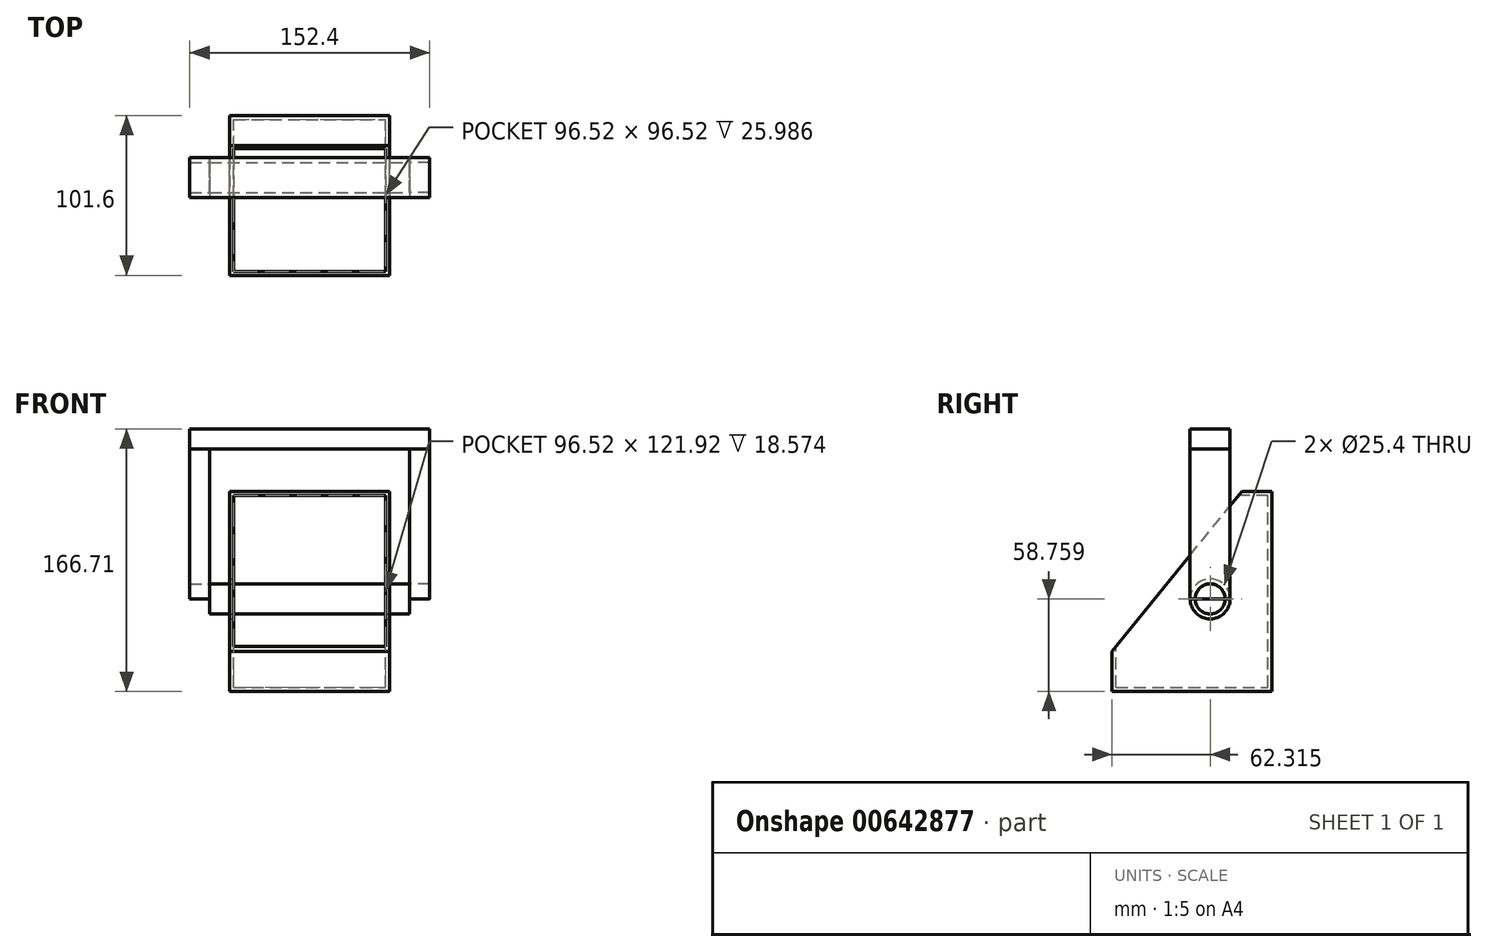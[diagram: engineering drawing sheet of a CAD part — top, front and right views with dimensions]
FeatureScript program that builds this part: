
annotation { "Feature Type Name" : "Feature", "Feature Type Description" : "" }
export const myFeature = defineFeature(function(context is Context, id is Id, definition is map)
    precondition{}
    {
        {
            var Q0;
            Q0=qCreatedBy(makeId("Right.planeOp"),FACE);
            var sketch = newSketch(context, id + "F0", { "sketchPlane" : qUnion([Q0])});
            skLineSegment(sketch, "E0", {"start": v(0, 0) * mm, "end": v(101.6, 0) * mm});
            skLineSegment(sketch, "E1", {"start": v(101.6, 0) * mm, "end": v(101.6, 127) * mm});
            skLineSegment(sketch, "E2", {"start": v(101.6, 127) * mm, "end": v(82.55, 127) * mm});
            skLineSegment(sketch, "E3", {"start": v(0, 0) * mm, "end": v(0, 25.4) * mm});
            skLineSegment(sketch, "E4", {"start": v(0, 25.4) * mm, "end": v(82.55, 127) * mm});
            skSolve(sketch);
        }
        {
            var Q0;
            Q0=makeQuery(id+"F0.imprint","IMPRINT",FACE,{"disambiguationData":[TD([[makeQuery(id+"F0.imprint","IMPRINT",EDGE,{"derivedFrom":sQuery(id+"F0.wireOp",EDGE,"E0")}),1.0]])]});
            extrude(context, id + "F1", {"entities" : qUnion([Q0]), "oppositeDirection" : true, "depth" : 101.6 * mm, "offsetDistance" : 25.4 * mm});
        }
        {
            var Q0;
            Q0=makeQuery(id+"F1.opExtrude","SWEPT_FACE",FACE,{"disambiguationData":[OSD([sQuery(id+"F0.wireOp",EDGE,"E4")])]});
            shell(context, id + "F2", {"entities" : qUnion([Q0]), "thickness" : 2.54 * mm});
        }
        {
            var Q0;
            Q0=makeQuery(id+"F1.opExtrude","CAP_FACE",FACE,{"disambiguationData":[OSD([sQuery(id+"F0.wireOp",EDGE,"E0"),sQuery(id+"F0.wireOp",EDGE,"E1"),sQuery(id+"F0.wireOp",EDGE,"E2"),sQuery(id+"F0.wireOp",EDGE,"E3"),sQuery(id+"F0.wireOp",EDGE,"E4")])],"isStart":true});
            var sketch = newSketch(context, id + "F3", { "sketchPlane" : qUnion([Q0])});
            skCircle(sketch, "E5", {"center": v(62.31, 58.76) * mm, "radius": 12.7 * mm});
            skSolve(sketch);
        }
        {
            var Q0;
            Q0=makeQuery(id+"F3.imprint","IMPRINT",FACE,{"disambiguationData":[TD([[makeQuery(id+"F3.imprint","IMPRINT",EDGE,{"derivedFrom":sQuery(id+"F3.wireOp",EDGE,"E5")}),1.0]])]});
            extrude(context, id + "F4", {"entities" : qUnion([Q0]), "operationType" : NewBodyOperationType.REMOVE, "oppositeDirection" : true, "depth" : 101.6 * mm, "offsetDistance" : 25.4 * mm});
        }
        {
            var Q0;
            Q0=makeQuery(id+"F1.opExtrude","CAP_FACE",FACE,{"disambiguationData":[OSD([sQuery(id+"F0.wireOp",EDGE,"E0"),sQuery(id+"F0.wireOp",EDGE,"E1"),sQuery(id+"F0.wireOp",EDGE,"E2"),sQuery(id+"F0.wireOp",EDGE,"E3"),sQuery(id+"F0.wireOp",EDGE,"E4")])],"isStart":true});
            var sketch = newSketch(context, id + "F5", { "sketchPlane" : qUnion([Q0])});
            skCircle(sketch, "E6", {"center": v(62.31, 58.76) * mm, "radius": 9.53 * mm});
            skSolve(sketch);
        }
        {
            var Q0;
            Q0=makeQuery(id+"F5.imprint","IMPRINT",FACE,{"disambiguationData":[TD([[makeQuery(id+"F5.imprint","IMPRINT",EDGE,{"derivedFrom":sQuery(id+"F5.wireOp",EDGE,"E6")}),1.0]])]});
            extrude(context, id + "F6", {"entities" : qUnion([Q0]), "oppositeDirection" : true, "depth" : 114.3 * mm, "offsetDistance" : 25.4 * mm});
        }
        {
            var Q0;
            Q0=makeQuery(id+"F6.opExtrude","CAP_FACE",FACE,{"disambiguationData":[OSD([sQuery(id+"F5.wireOp",EDGE,"E6")])],"isStart":true});
            extrude(context, id + "F7", {"entities" : qUnion([Q0]), "operationType" : NewBodyOperationType.ADD, "depth" : 12.7 * mm, "offsetDistance" : 25.4 * mm});
        }
        {
            var Q0;
            Q0=makeQuery(id+"F7.opExtrude","CAP_FACE",FACE,{"disambiguationData":[OSD([sQuery(id+"F5.wireOp",EDGE,"E6")])],"isStart":false});
            var sketch = newSketch(context, id + "F8", { "sketchPlane" : qUnion([Q0])});
            skLineSegment(sketch, "E7", {"start": v(62.31, 58.76) * mm, "end": v(75.01, 58.76) * mm});
            skLineSegment(sketch, "E8", {"start": v(62.31, 58.76) * mm, "end": v(49.61, 58.76) * mm});
            skLineSegment(sketch, "E9", {"start": v(49.61, 58.76) * mm, "end": v(49.61, 154) * mm});
            skLineSegment(sketch, "E10", {"start": v(75.01, 58.76) * mm, "end": v(75.01, 154) * mm});
            skLineSegment(sketch, "E11", {"start": v(75.01, 154) * mm, "end": v(49.61, 154) * mm});
            skSolve(sketch);
        }
        {
            var Q0;
            {var subQ1=sQuery(id+"F8.wireOp",EDGE,"E9");Q0=makeQuery(id+"F8.imprint","IMPRINT",FACE,{"disambiguationData":[TD([[makeQuery(id+"F8.imprint","IMPRINT",EDGE,{"derivedFrom":subQ1}),-1.0]])]});}
            extrude(context, id + "F9", {"entities" : qUnion([Q0]), "depth" : 12.7 * mm, "offsetDistance" : 25.4 * mm});
        }
        {
            var Q0;
            Q0=makeQuery(id+"F7.opExtrude","CAP_FACE",FACE,{"disambiguationData":[OSD([sQuery(id+"F5.wireOp",EDGE,"E6")])],"isStart":false});
            var sketch = newSketch(context, id + "F10", { "sketchPlane" : qUnion([Q0])});
            skLineSegment(sketch, "E12", {"start": v(52.79, 58.75) * mm, "end": v(71.84, 58.75) * mm});
            skSolve(sketch);
        }
        {
            var Q0;
            {var subQ0=sQuery(id+"F10.wireOp",EDGE,"E12");Q0=makeQuery(id+"F10.imprint","IMPRINT",FACE,{"disambiguationData":[TD([[makeQuery(id+"F10.imprint","IMPRINT",EDGE,{"derivedFrom":subQ0}),1.0]])]});}
            extrude(context, id + "F11", {"entities" : qUnion([Q0]), "depth" : 12.7 * mm, "offsetDistance" : 25.4 * mm});
        }
        {
            var Q0;
            Q0=makeQuery(id+"F6.opExtrude","CAP_FACE",FACE,{"disambiguationData":[OSD([sQuery(id+"F5.wireOp",EDGE,"E6")])],"isStart":false});
            var sketch = newSketch(context, id + "F12", { "sketchPlane" : qUnion([Q0])});
            skLineSegment(sketch, "E13", {"start": v(-62.31, 58.76) * mm, "end": v(-49.61, 58.76) * mm});
            skLineSegment(sketch, "E14", {"start": v(-49.61, 58.76) * mm, "end": v(-75, 58.76) * mm});
            skLineSegment(sketch, "E15", {"start": v(-75, 58.76) * mm, "end": v(-75, 154) * mm});
            skLineSegment(sketch, "E16", {"start": v(-49.61, 58.76) * mm, "end": v(-49.61, 154) * mm});
            skLineSegment(sketch, "E17", {"start": v(-75, 154) * mm, "end": v(-49.61, 154) * mm});
            skSolve(sketch);
        }
        {
            var Q0;
            {var subQ0=sQuery(id+"F12.wireOp",EDGE,"E15");Q0=makeQuery(id+"F12.imprint","IMPRINT",FACE,{"disambiguationData":[TD([[makeQuery(id+"F12.imprint","IMPRINT",EDGE,{"derivedFrom":subQ0}),-1.0]])]});}
            extrude(context, id + "F13", {"entities" : qUnion([Q0]), "depth" : 12.7 * mm, "offsetDistance" : 25.4 * mm});
        }
        {
            var Q0;
            Q0=makeQuery(id+"F6.opExtrude","CAP_FACE",FACE,{"disambiguationData":[OSD([sQuery(id+"F5.wireOp",EDGE,"E6")])],"isStart":false});
            var sketch = newSketch(context, id + "F14", { "sketchPlane" : qUnion([Q0])});
            skLineSegment(sketch, "E18", {"start": v(-62.31, 58.76) * mm, "end": v(-71.84, 58.76) * mm});
            skLineSegment(sketch, "E19", {"start": v(-71.84, 58.76) * mm, "end": v(-52.79, 58.76) * mm});
            skSolve(sketch);
        }
        {
            var Q0;
            {var subQ0=sQuery(id+"F14.wireOp",EDGE,"E19");var subQ3=makeQuery(id+"F14.imprint","IMPRINT",VERTEX,{"derivedFrom":subQ0});Q0=makeQuery(id+"F14.imprint","IMPRINT",FACE,{"disambiguationData":[TD([[makeQuery(id+"F14.imprint","IMPRINT",EDGE,{"disambiguationData":[TD([[subQ3,1.0]])],"derivedFrom":subQ0}),1.0]])]});}
            extrude(context, id + "F15", {"entities" : qUnion([Q0]), "depth" : 12.7 * mm, "offsetDistance" : 25.4 * mm});
        }
        {
            var Q0;
            Q0=makeQuery(id+"F13.opExtrude","SWEPT_FACE",FACE,{"disambiguationData":[OSD([sQuery(id+"F12.wireOp",EDGE,"E16")])]});
            var sketch = newSketch(context, id + "F16", { "sketchPlane" : qUnion([Q0])});
            skLineSegment(sketch, "E20", {"start": v(-127, 154) * mm, "end": v(-127, 166.7) * mm});
            skLineSegment(sketch, "E21", {"start": v(-127, 166.7) * mm, "end": v(25.4, 166.7) * mm});
            skLineSegment(sketch, "E22", {"start": v(25.4, 166.7) * mm, "end": v(25.4, 154) * mm});
            skLineSegment(sketch, "E23", {"start": v(25.4, 154) * mm, "end": v(-127, 154) * mm});
            skSolve(sketch);
        }
        {
            var Q0;
            {var subQ4=sQuery(id+"F16.wireOp",EDGE,"E20");Q0=makeQuery(id+"F16.imprint","IMPRINT",FACE,{"disambiguationData":[TD([[makeQuery(id+"F16.imprint","IMPRINT",EDGE,{"derivedFrom":subQ4}),-1.0]])]});}
            extrude(context, id + "F17", {"entities" : qUnion([Q0]), "oppositeDirection" : true, "depth" : 25.4 * mm, "offsetDistance" : 25.4 * mm});
        }
    });
